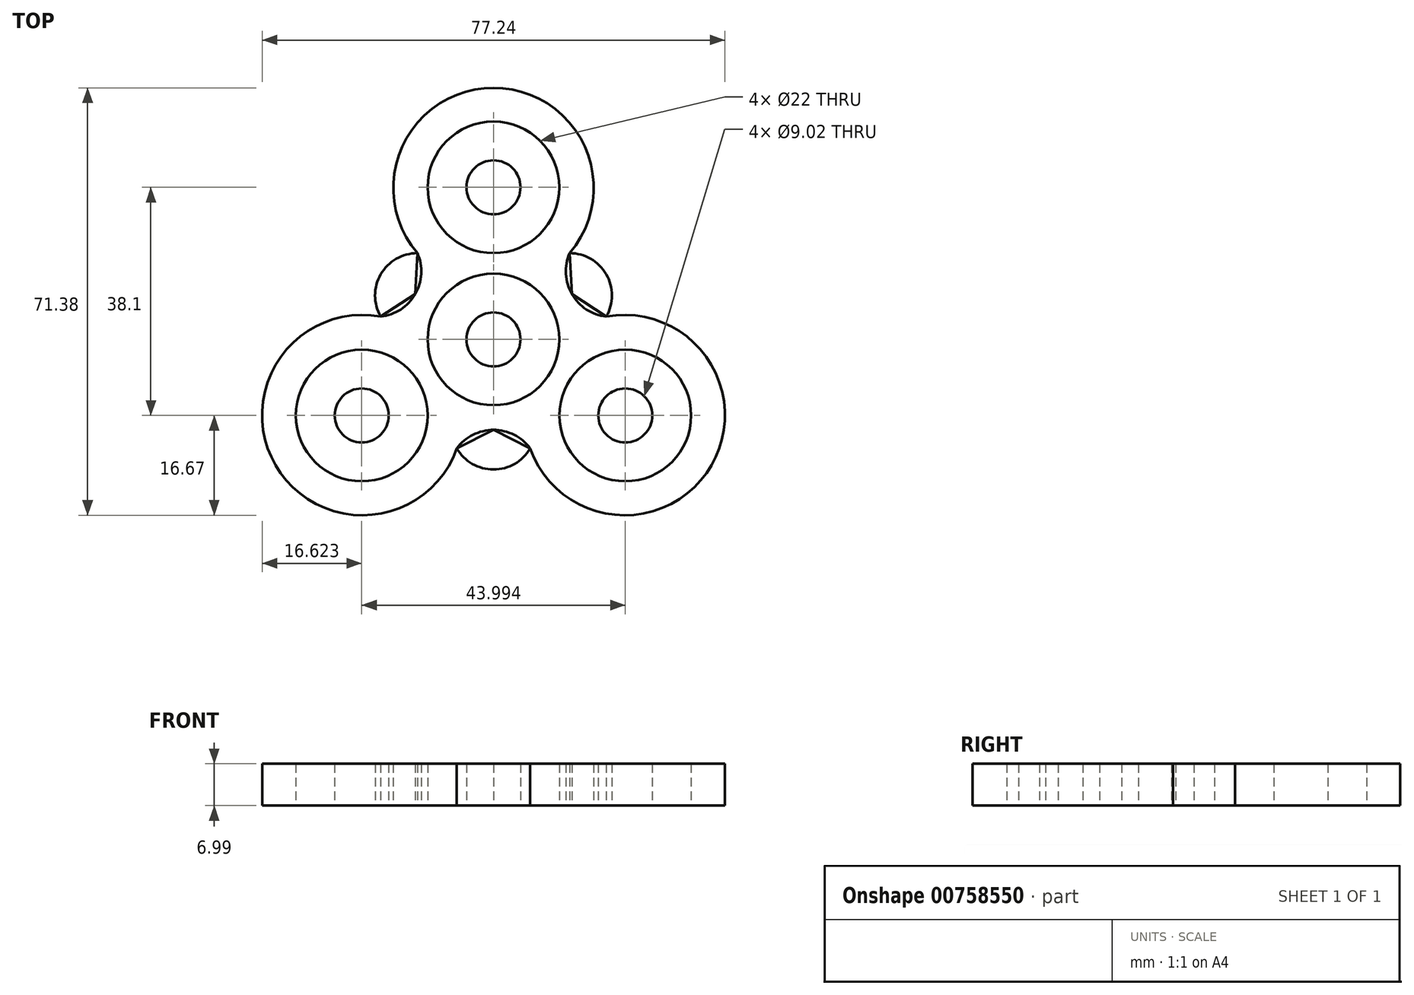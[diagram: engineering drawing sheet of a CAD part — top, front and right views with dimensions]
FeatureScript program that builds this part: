
annotation { "Feature Type Name" : "Feature", "Feature Type Description" : "" }
export const myFeature = defineFeature(function(context is Context, id is Id, definition is map)
    precondition{}
    {
        {
            var Q0;
            Q0=qCreatedBy(makeId("Top.planeOp"),FACE);
            var sketch = newSketch(context, id + "F0", { "sketchPlane" : qUnion([Q0])});
            skLineSegment(sketch, "E0", {"start": v(0, 0) * mm, "end": v(22, -12.7) * mm, "construction": true});
            skLineSegment(sketch, "E1", {"start": v(0, 0) * mm, "end": v(-22, -12.7) * mm, "construction": true});
            skCircle(sketch, "E2", {"center": v(-22, -12.7) * mm, "radius": 4.5 * mm});
            skCircle(sketch, "E3", {"center": v(-22, -12.7) * mm, "radius": 11 * mm});
            skCircle(sketch, "E4", {"center": v(22, -12.7) * mm, "radius": 4.5 * mm});
            skCircle(sketch, "E5", {"center": v(22, -12.7) * mm, "radius": 11 * mm});
            skLineSegment(sketch, "E6", {"start": v(0, 0) * mm, "end": v(0, 25.4) * mm, "construction": true});
            skCircle(sketch, "E7", {"center": v(0, 25.4) * mm, "radius": 4.5 * mm});
            skCircle(sketch, "E8", {"center": v(0, 25.4) * mm, "radius": 11 * mm});
            skCircle(sketch, "E9", {"center": v(0, 0) * mm, "radius": 4.5 * mm});
            skCircle(sketch, "E10", {"center": v(0, 0) * mm, "radius": 11 * mm});
            skLineSegment(sketch, "E11", {"start": v(-12.47, -7.2) * mm, "end": v(-18.82, 3.8) * mm, "construction": true});
            skLineSegment(sketch, "E12", {"start": v(12.47, -7.2) * mm, "end": v(18.82, 3.8) * mm, "construction": true});
            skLineSegment(sketch, "E13", {"start": v(0, 14.4) * mm, "end": v(12.7, 14.4) * mm, "construction": true});
            skLineSegment(sketch, "E14", {"start": v(0, 14.4) * mm, "end": v(-12.7, 14.4) * mm, "construction": true});
            skLineSegment(sketch, "E15", {"start": v(-12.47, -7.2) * mm, "end": v(-6.12, -18.2) * mm, "construction": true});
            skLineSegment(sketch, "E16", {"start": v(12.47, -7.2) * mm, "end": v(6.12, -18.2) * mm, "construction": true});
            skArc(sketch, "E17", {"start": v(-18.82, 3.8) * mm, "mid": v(-36.38, -21) * mm, "end": v(-6.12, -18.2) * mm});
            skArc(sketch, "E18", {"start": v(6.12, -18.2) * mm, "mid": v(36.38, -21) * mm, "end": v(18.82, 3.8) * mm});
            skArc(sketch, "E19", {"start": v(12.7, 14.4) * mm, "mid": v(0, 42) * mm, "end": v(-12.7, 14.4) * mm});
            skArc(sketch, "E20", {"start": v(12.7, 14.4) * mm, "mid": v(13.1, 7.56) * mm, "end": v(18.82, 3.8) * mm});
            skArc(sketch, "E21", {"start": v(6.12, -18.2) * mm, "mid": v(0, -15.12) * mm, "end": v(-6.12, -18.2) * mm});
            skArc(sketch, "E22", {"start": v(-18.82, 3.8) * mm, "mid": v(-13.1, 7.56) * mm, "end": v(-12.7, 14.4) * mm});
            skArc(sketch, "E23", {"start": v(18.82, 3.8) * mm, "mid": v(18.82, 10.87) * mm, "end": v(12.7, 14.4) * mm});
            skArc(sketch, "E24", {"start": v(-6.12, -18.2) * mm, "mid": v(0, -21.73) * mm, "end": v(6.12, -18.2) * mm});
            skArc(sketch, "E25", {"start": v(-12.7, 14.4) * mm, "mid": v(-18.82, 10.87) * mm, "end": v(-18.82, 3.8) * mm});
            skLineSegment(sketch, "E26", {"start": v(-6.12, -18.2) * mm, "end": v(0, -15.12) * mm});
            skLineSegment(sketch, "E27", {"start": v(0, -15.12) * mm, "end": v(6.12, -18.2) * mm});
            skLineSegment(sketch, "E28", {"start": v(-18.82, 3.8) * mm, "end": v(-13.1, 7.56) * mm});
            skLineSegment(sketch, "E29", {"start": v(-13.1, 7.56) * mm, "end": v(-12.7, 14.4) * mm});
            skLineSegment(sketch, "E30", {"start": v(12.7, 14.4) * mm, "end": v(13.1, 7.56) * mm});
            skLineSegment(sketch, "E31", {"start": v(13.1, 7.56) * mm, "end": v(18.82, 3.8) * mm});
            skSolve(sketch);
        }
        {
            var Q0;
            Q0=makeQuery(id+"F0.imprint","IMPRINT",FACE,{"disambiguationData":[TD([[makeQuery(id+"F0.imprint","IMPRINT",EDGE,{"derivedFrom":sQuery(id+"F0.wireOp",EDGE,"E2")}),-1.0]])]});
            var Q1;
            Q1=makeQuery(id+"F0.imprint","IMPRINT",FACE,{"disambiguationData":[TD([[makeQuery(id+"F0.imprint","IMPRINT",EDGE,{"derivedFrom":sQuery(id+"F0.wireOp",EDGE,"E4")}),-1.0]])]});
            extrude(context, id + "F1", {"entities" : qUnion([Q0, Q1]), "depth" : 7 * mm, "offsetDistance" : 25.4 * mm});
        }
        {
            var Q0;
            Q0=makeQuery(id+"F0.imprint","IMPRINT",FACE,{"disambiguationData":[TD([[makeQuery(id+"F0.imprint","IMPRINT",EDGE,{"derivedFrom":sQuery(id+"F0.wireOp",EDGE,"E7")}),-1.0]])]});
            extrude(context, id + "F2", {"entities" : qUnion([Q0]), "depth" : 7 * mm, "offsetDistance" : 25.4 * mm});
        }
        {
            var Q0;
            Q0=makeQuery(id+"F0.imprint","IMPRINT",FACE,{"disambiguationData":[TD([[makeQuery(id+"F0.imprint","IMPRINT",EDGE,{"derivedFrom":sQuery(id+"F0.wireOp",EDGE,"E9")}),-1.0]])]});
            extrude(context, id + "F3", {"entities" : qUnion([Q0]), "depth" : 7 * mm, "offsetDistance" : 25.4 * mm});
        }
        {
            var Q0;
            Q0=makeQuery(id+"F0.imprint","IMPRINT",FACE,{"disambiguationData":[TD([[makeQuery(id+"F0.imprint","IMPRINT",EDGE,{"derivedFrom":sQuery(id+"F0.wireOp",EDGE,"E3")}),-1.0]])]});
            extrude(context, id + "F4", {"entities" : qUnion([Q0]), "depth" : 7 * mm, "offsetDistance" : 25.4 * mm});
        }
        {
            var Q0;
            Q0=makeQuery(id+"F0.imprint","IMPRINT",FACE,{"disambiguationData":[TD([[makeQuery(id+"F0.imprint","IMPRINT",EDGE,{"derivedFrom":sQuery(id+"F0.wireOp",EDGE,"E25")}),1.0]])]});
            var Q1;
            Q1=makeQuery(id+"F0.imprint","IMPRINT",FACE,{"disambiguationData":[TD([[makeQuery(id+"F0.imprint","IMPRINT",EDGE,{"derivedFrom":sQuery(id+"F0.wireOp",EDGE,"E23")}),1.0]])]});
            var Q2;
            Q2=makeQuery(id+"F0.imprint","IMPRINT",FACE,{"disambiguationData":[TD([[makeQuery(id+"F0.imprint","IMPRINT",EDGE,{"derivedFrom":sQuery(id+"F0.wireOp",EDGE,"E24")}),1.0]])]});
            extrude(context, id + "F5", {"entities" : qUnion([Q0, Q1, Q2]), "depth" : 7 * mm, "offsetDistance" : 25.4 * mm});
        }
    });
